# Revit family: CE43
name_source: partatom
category: Attrezzature speciali
revit_build: Autodesk Revit 2017 (Build: 20160225_1515(x64)
units: mm (PartAtom-declared; Revit-internal decimal feet)

## family parameters
Basato su piano di lavoro = No
Condiviso = No
Punto di calcolo locali = No
Quota connettore circolare = Usa diametro
Sempre verticale = Sì
Taglio con vuoti quando caricato = No
Tipo di parte = Normale

## types (2) — shared parameters
230 Volt = Sì
Apparent power = 3060 VA
Capacity factor = 80.00%
Clearance = 270 mm  [stored 0.885827 ft]
Electrical supply = 230 V
Height = 670 mm  [stored 2.19816 ft]
Installed Load = 3.1 kW
Latent Heat = 0.13 kW
Length = 521 mm  [stored 1.70932 ft]
Output racks/h = 40
Overall size = 851 mm  [stored 2.79199 ft]
Rack size = 350 X 350
Sensible Heat = 0.77 kW
Tank drain = 35 mm  [stored 0.114829 ft]
Total absorption = 12 A
Water inlet = 1"
Width = 430 mm

## per-type parameters (varying)
| type | Rinse water consumption | Water softener |
| CE43 | 2.0 L | No |
| CE43A | 2.5 L | Sì |

note: [stored X ft] marks values corroborated as IEEE doubles in the binary element streams (Revit-internal decimal feet)

## geometry (parser evidence)
native form markers: Blend x2
no freeform markers — native parametric forms only
